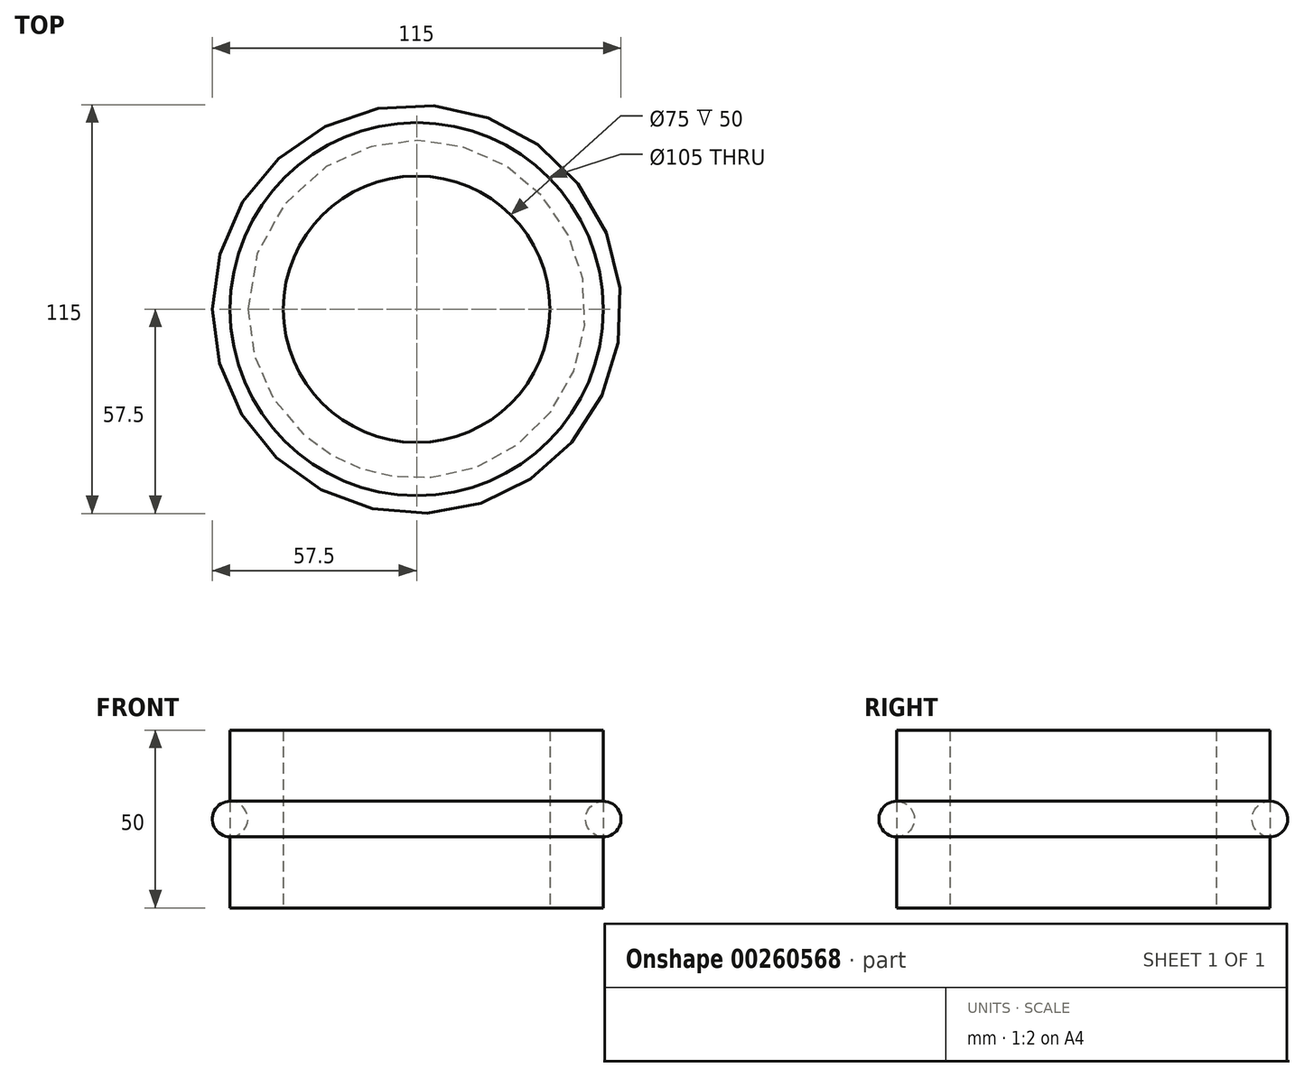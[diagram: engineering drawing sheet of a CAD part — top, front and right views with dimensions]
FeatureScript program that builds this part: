
annotation { "Feature Type Name" : "Feature", "Feature Type Description" : "" }
export const myFeature = defineFeature(function(context is Context, id is Id, definition is map)
    precondition{}
    {
        {
            var Q0;
            Q0=qCreatedBy(makeId("Front.planeOp"),FACE);
            var sketch = newSketch(context, id + "F0", { "sketchPlane" : qUnion([Q0])});
            skLineSegment(sketch, "E0", {"start": v(0, 0) * mm, "end": v(0, 50) * mm, "construction": true});
            skLineSegment(sketch, "E1.bottom", {"start": v(37.5, 0) * mm, "end": v(52.5, 0) * mm});
            skLineSegment(sketch, "E1.top", {"start": v(37.5, 50) * mm, "end": v(52.5, 50) * mm});
            skLineSegment(sketch, "E1.left", {"start": v(37.5, 0) * mm, "end": v(37.5, 50) * mm});
            skLineSegment(sketch, "E1.right", {"start": v(52.5, 0) * mm, "end": v(52.5, 50) * mm});
            skCircle(sketch, "E2", {"center": v(52.5, 25) * mm, "radius": 5 * mm});
            skSolve(sketch);
        }
        {
            var Q0;
            {var subQ1=sQuery(id+"F0.wireOp",EDGE,"E1.bottom");Q0=makeQuery(id+"F0.imprint","IMPRINT",FACE,{"disambiguationData":[TD([[makeQuery(id+"F0.imprint","IMPRINT",EDGE,{"derivedFrom":subQ1}),1.0]])]});}
            var Q1;
            {var subQ0=sQuery(id+"F0.wireOp",EDGE,"E2");var subQ1=sQuery(id+"F0.wireOp",EDGE,"E1.right");var subQ2=makeQuery(id+"F0.imprint","INTERSECT",VERTEX,{"disambiguationData":[OD(0.0)],"derivedFrom":[subQ1,subQ0]});Q1=makeQuery(id+"F0.imprint","IMPRINT",FACE,{"disambiguationData":[TD([[makeQuery(id+"F0.imprint","IMPRINT",EDGE,{"disambiguationData":[TD([[subQ2,-1.0]])],"derivedFrom":subQ1}),-1.0]])]});}
            var Q2;
            Q2=sQuery(id+"F0.wireOp",EDGE,"E0");
            revolve(context, id + "F1", {"entities" : qUnion([Q0, Q1]), "axis" : qUnion([Q2]), "revolveType" : RevolveType.FULL});
        }
    });
